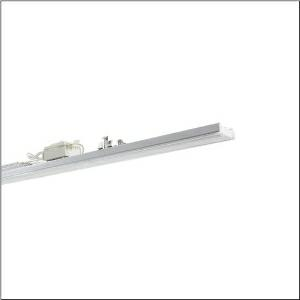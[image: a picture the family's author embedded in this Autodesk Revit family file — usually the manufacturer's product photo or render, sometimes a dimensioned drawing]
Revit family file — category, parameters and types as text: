
# Revit family: licross_r__21_recessed_mo_52te12dn4axg3s_3072
name_source: partatom
category: Lighting Fixtures
units: mm (PartAtom-declared; Revit-internal decimal feet)

## family parameters
Cut with Voids When Loaded = No
Host = Face
Light Source = No
Part Type = Normal
Room Calculation Point = No
Round Connector Dimension = Use Diameter
Shared = No

## types (1)
- --- (1 x LED, 950 lm, 6.7 W, 4000K)
    Apparent Load = 7 VA
    CIE Flux Codes = 72 92 99 100 100
    Color Rendering = 80
    Color Temperature = 4000K
    Default Elevation = 1800 mm
    Description = Licross® 21 Recessed MO, luminaire insert, of sheet steel, galvanised, coil coated, white, length: 1.500mm, width: 66mm, height: 67mm, LED rated luminous flux: 10.280lm, light colour: 840, control gear: DALI 2 (for two DALI lines), with plug, 6-pole, with phase selection, for trunking rail, 14-core, mains connection: 220..240V, AC, 50/60Hz, rated input power: 62W, halogen-free wiring, for emergency light function, for trunking rail, 14-core, converter,control gear: single battery element, battery: LiFePO4, 9Ah, primary optical cover: cover, of PMMA, light emission: direct distribution, primary light characteristic: symmetric, protection rating (complete): IP54, insulation class (complete): insulation class I (protective earthing), certification: CE, UKCA, protection symbol: D if used in an environment with non-conductive dust loads with corresponding accessories, impact resistance: IK06, permissible ambient temperature for indoor applications: +5..+35°C, standard: EN 60598-2-22, LABS conformity tested according to VDMA 24364:2018-05, reducing of maximum allowable ambient temperature of 5°C with ceiling mounting, corresponds to IFS (International Featured Standards) requirements for safety and quality in the food industry, packaging unit: 1 piece
    Height = 58 mm
    Lamp = 1 x LED
    Lamp Light Flux = 950 lm
    Lamp Power = 6.7 W
    Lamp count = 1
    Length = 1500 mm
    Luminous efficacy = 142 lm/W
    Manufacturer = Siteco
    ModVariant = No
    Model = 52TE12DN4AXG3S
    Mounting Place = Ceiling
    Mounting Type = Pendant
    Number of Poles = 1
    OnlyDefault = Yes
    Power Factor = 1
    Product Name = Licross® 21 Recessed MO
    Product group = luminaire insert
    ProductGroupID = 902
    Protection Class = Protection class I
    Protection Degree = IP 54
    RLX_Detail_Level = 1
    RLX_Emergency_Light_Flux = 0 lm
    RLX_Emergency_Type = 0
    RLX_Emergency_Type_DB = No
    RlxData = <blob elided: 25041 chars, md5=7e300ac5>
    Socket = socket
    Standby Power = 0 W
    System Light Flux = 950 lm
    System Power = 7 W
    Type Comments = : emergency light operation: 3 h
    Type Image = l_1296930.jpg
    URL = http://relux.com
    VarID = @adj_110058
    Voltage = 0 V
    Weight = 0.00 kg
    Width = 66 mm

## geometry (parser evidence)
native form markers: Blend x4, Sweep x10
no freeform markers — native parametric forms only
